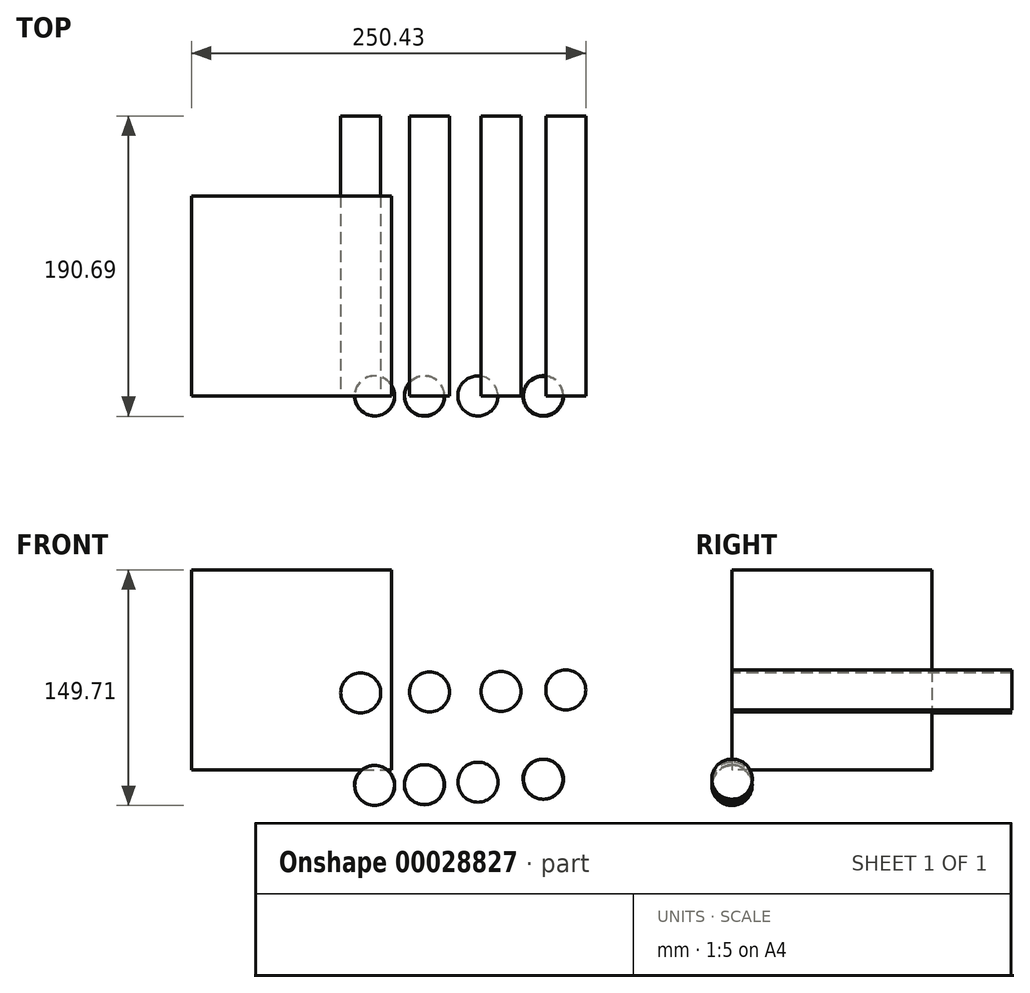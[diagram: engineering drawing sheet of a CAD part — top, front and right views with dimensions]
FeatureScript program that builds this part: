
annotation { "Feature Type Name" : "Feature", "Feature Type Description" : "" }
export const myFeature = defineFeature(function(context is Context, id is Id, definition is map)
    precondition{}
    {
        {
            var Q0;
            Q0=qCreatedBy(makeId("Front.planeOp"),FACE);
            var sketch = newSketch(context, id + "F0", { "sketchPlane" : qUnion([Q0])});
            skLineSegment(sketch, "E0.bottom", {"start": v(-31.13, 90.1) * mm, "end": v(95.87, 90.1) * mm});
            skLineSegment(sketch, "E0.top", {"start": v(-31.13, -36.9) * mm, "end": v(95.87, -36.9) * mm});
            skLineSegment(sketch, "E0.left", {"start": v(-31.13, 90.1) * mm, "end": v(-31.13, -36.9) * mm});
            skLineSegment(sketch, "E0.right", {"start": v(95.87, 90.1) * mm, "end": v(95.87, -36.9) * mm});
            skSolve(sketch);
        }
        {
            var Q0;
            Q0 = qSketchRegion(id + "F0", true);
            extrude(context, id + "F1", {"entities" : qUnion([Q0]), "oppositeDirection" : true, "depth" : 127 * mm});
        }
        {
            var Q0;
            Q0=qCreatedBy(makeId("Front.planeOp"),FACE);
            var sketch = newSketch(context, id + "F2", { "sketchPlane" : qUnion([Q0])});
            skCircle(sketch, "E1", {"center": v(76.37, 11.88) * mm, "radius": 12.7 * mm});
            skCircle(sketch, "E2", {"center": v(120.1, 12.52) * mm, "radius": 12.7 * mm});
            skCircle(sketch, "E3", {"center": v(165.4, 12.83) * mm, "radius": 12.7 * mm});
            skCircle(sketch, "E4", {"center": v(206.6, 13.78) * mm, "radius": 12.7 * mm});
            skSolve(sketch);
        }
        {
            var Q0;
            Q0 = qSketchRegion(id + "F2", true);
            extrude(context, id + "F3", {"entities" : qUnion([Q0]), "oppositeDirection" : true, "depth" : 177.8 * mm});
        }
        {
            var Q0;
            Q0=qCreatedBy(makeId("Front.planeOp"),FACE);
            var sketch = newSketch(context, id + "F4", { "sketchPlane" : qUnion([Q0])});
            skLineSegment(sketch, "E5", {"start": v(85.18, -34.2) * mm, "end": v(85.18, -59.6) * mm});
            skLineSegment(sketch, "E6", {"start": v(116.86, -33.7) * mm, "end": v(116.86, -59.1) * mm});
            skLineSegment(sketch, "E7", {"start": v(150.77, -32.11) * mm, "end": v(150.77, -57.51) * mm});
            skLineSegment(sketch, "E8", {"start": v(192.28, -30.21) * mm, "end": v(192.28, -55.61) * mm});
            skArc(sketch, "E9", {"start": v(85.18, -34.2) * mm, "mid": v(72.39, -46.9) * mm, "end": v(85.18, -59.6) * mm});
            skArc(sketch, "E10", {"start": v(116.86, -33.7) * mm, "mid": v(104.05, -46.4) * mm, "end": v(116.86, -59.1) * mm});
            skArc(sketch, "E11", {"start": v(150.77, -32.11) * mm, "mid": v(138.07, -44.81) * mm, "end": v(150.77, -57.51) * mm});
            skArc(sketch, "E12", {"start": v(192.28, -30.21) * mm, "mid": v(179.76, -42.91) * mm, "end": v(192.28, -55.61) * mm});
            skSolve(sketch);
        }
        {
            var Q0;
            Q0=makeQuery(id+"F4.imprint","IMPRINT",FACE,{"disambiguationData":[TD([[makeQuery(id+"F4.imprint","IMPRINT",EDGE,{"derivedFrom":sQuery(id+"F4.wireOp",EDGE,"E5")}),-1.0]])]});
            var Q1;
            Q1=sQuery(id+"F4.wireOp",EDGE,"E5");
            revolve(context, id + "F5", {"entities" : qUnion([Q0]), "axis" : qUnion([Q1]), "revolveType" : RevolveType.FULL});
        }
        {
            var Q0;
            Q0=makeQuery(id+"F4.imprint","IMPRINT",FACE,{"disambiguationData":[TD([[makeQuery(id+"F4.imprint","IMPRINT",EDGE,{"derivedFrom":sQuery(id+"F4.wireOp",EDGE,"E6")}),-1.0]])]});
            var Q1;
            Q1=sQuery(id+"F4.wireOp",EDGE,"E6");
            revolve(context, id + "F6", {"entities" : qUnion([Q0]), "axis" : qUnion([Q1]), "revolveType" : RevolveType.FULL});
        }
        {
            var Q0;
            Q0=makeQuery(id+"F4.imprint","IMPRINT",FACE,{"disambiguationData":[TD([[makeQuery(id+"F4.imprint","IMPRINT",EDGE,{"derivedFrom":sQuery(id+"F4.wireOp",EDGE,"E7")}),-1.0]])]});
            var Q1;
            Q1=sQuery(id+"F4.wireOp",EDGE,"E7");
            revolve(context, id + "F7", {"entities" : qUnion([Q0]), "axis" : qUnion([Q1]), "revolveType" : RevolveType.FULL});
        }
        {
            var Q0;
            Q0=makeQuery(id+"F4.imprint","IMPRINT",FACE,{"disambiguationData":[TD([[makeQuery(id+"F4.imprint","IMPRINT",EDGE,{"derivedFrom":sQuery(id+"F4.wireOp",EDGE,"E8")}),-1.0]])]});
            var Q1;
            Q1=sQuery(id+"F4.wireOp",EDGE,"E8");
            revolve(context, id + "F8", {"entities" : qUnion([Q0]), "axis" : qUnion([Q1]), "revolveType" : RevolveType.FULL});
        }
    });
